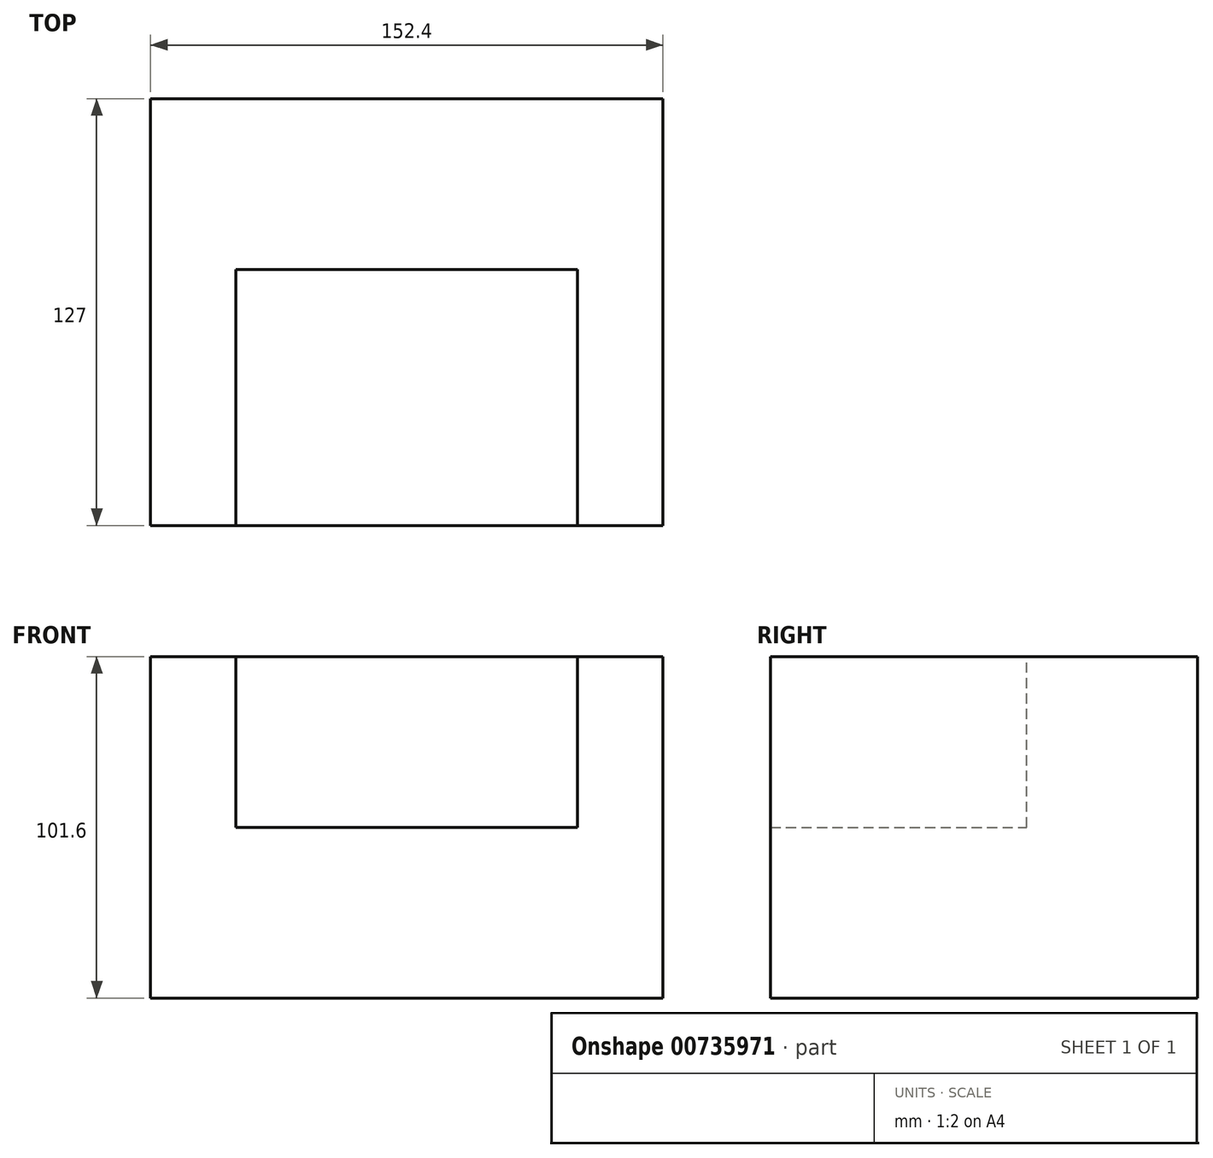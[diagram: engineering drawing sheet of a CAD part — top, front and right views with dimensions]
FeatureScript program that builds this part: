
annotation { "Feature Type Name" : "Feature", "Feature Type Description" : "" }
export const myFeature = defineFeature(function(context is Context, id is Id, definition is map)
    precondition{}
    {
        {
            var Q0;
            Q0=qCreatedBy(makeId("Front.planeOp"),FACE);
            var sketch = newSketch(context, id + "F0", { "sketchPlane" : qUnion([Q0])});
            skLineSegment(sketch, "E0.bottom", {"start": v(-200.66, 62.01) * mm, "end": v(-48.26, 62.01) * mm});
            skLineSegment(sketch, "E0.top", {"start": v(-200.66, -39.59) * mm, "end": v(-48.26, -39.59) * mm});
            skLineSegment(sketch, "E0.left", {"start": v(-200.66, 62.01) * mm, "end": v(-200.66, -39.59) * mm});
            skLineSegment(sketch, "E0.right", {"start": v(-48.26, 62.01) * mm, "end": v(-48.26, -39.59) * mm});
            skSolve(sketch);
        }
        {
            var Q0;
            Q0=makeQuery(id+"F0.imprint","IMPRINT",FACE,{"disambiguationData":[TD([[makeQuery(id+"F0.imprint","IMPRINT",EDGE,{"derivedFrom":sQuery(id+"F0.wireOp",EDGE,"E0.bottom")}),-1.0]])]});
            extrude(context, id + "F1", {"entities" : qUnion([Q0]), "depth" : 127 * mm, "offsetDistance" : 25.4 * mm});
        }
        {
            var Q0;
            Q0=makeQuery(id+"F1.opExtrude","SWEPT_FACE",FACE,{"disambiguationData":[OSD([sQuery(id+"F0.wireOp",EDGE,"E0.bottom")])]});
            var sketch = newSketch(context, id + "F2", { "sketchPlane" : qUnion([Q0])});
            skLineSegment(sketch, "E1.bottom", {"start": v(-175.26, -127) * mm, "end": v(-73.66, -127) * mm});
            skLineSegment(sketch, "E1.top", {"start": v(-175.26, -50.8) * mm, "end": v(-73.66, -50.8) * mm});
            skLineSegment(sketch, "E1.left", {"start": v(-175.26, -127) * mm, "end": v(-175.26, -50.8) * mm});
            skLineSegment(sketch, "E1.right", {"start": v(-73.66, -127) * mm, "end": v(-73.66, -50.8) * mm});
            skSolve(sketch);
        }
        {
            var Q0;
            Q0=makeQuery(id+"F2.imprint","IMPRINT",FACE,{"disambiguationData":[TD([[makeQuery(id+"F2.imprint","IMPRINT",EDGE,{"derivedFrom":sQuery(id+"F2.wireOp",EDGE,"E1.bottom")}),1.0]])]});
            extrude(context, id + "F3", {"entities" : qUnion([Q0]), "operationType" : NewBodyOperationType.REMOVE, "oppositeDirection" : true, "depth" : 50.8 * mm, "offsetDistance" : 25.4 * mm});
        }
    });
